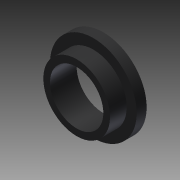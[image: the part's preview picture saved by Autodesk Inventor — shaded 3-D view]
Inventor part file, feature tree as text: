
AUTODESK INVENTOR PART (.ipt)
format: ipt  version: 2012 (Build 160160000, 160)  size: 86,016 bytes
history: native  units: in
note: dims shown in document units (in); Inventor stores cm internally (conversion verified against a paired STEP export)
features: extrude x2, sketch x1
ambient origin geometry x8: Origin, YZ Plane, XZ Plane, XY Plane, X Axis, Y Axis, Z Axis, Center Point
bodies: Solid1 (feature_tree)
feature tree (3):
  sketch  "Sketch1"  dims[d0=1.0in d1=1.25in d2=1.625in d3=0.5in d4=0.0in d5=0.1875in d6=0.0in]
  extrude  "Extrusion1"  Depth=1.25in
  extrude  "Extrusion2"  Depth=1.625in
